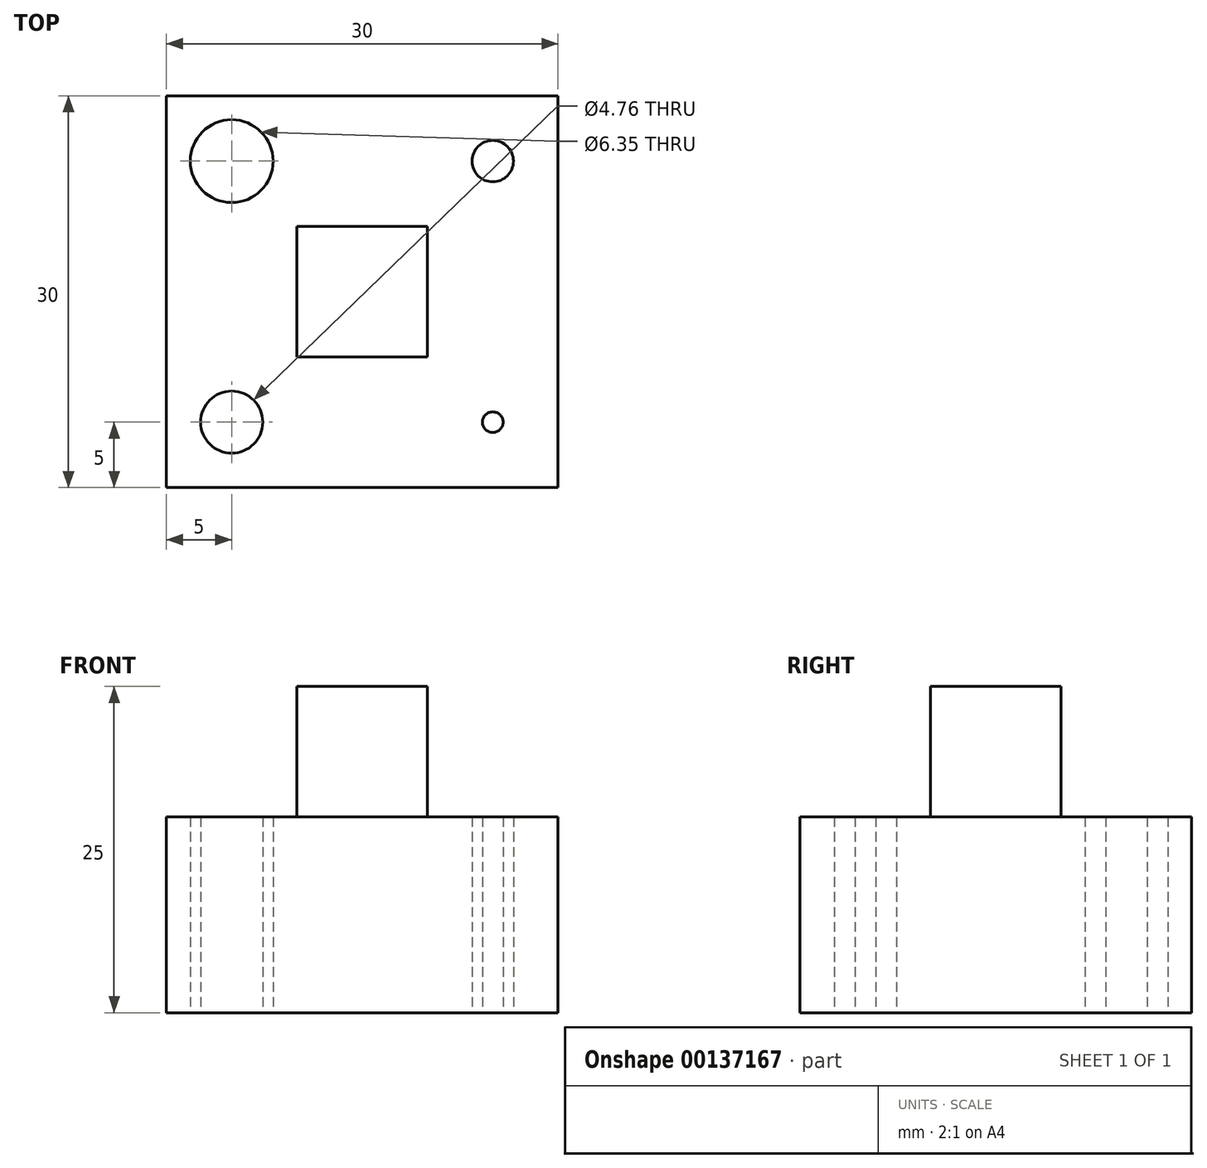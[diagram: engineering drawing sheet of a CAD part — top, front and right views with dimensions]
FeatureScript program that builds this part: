
annotation { "Feature Type Name" : "Feature", "Feature Type Description" : "" }
export const myFeature = defineFeature(function(context is Context, id is Id, definition is map)
    precondition{}
    {
        {
            var Q0;
            Q0=qCreatedBy(makeId("Top.planeOp"),FACE);
            var sketch = newSketch(context, id + "F0", { "sketchPlane" : qUnion([Q0])});
            skLineSegment(sketch, "E0.bottom", {"start": v(15, 15) * mm, "end": v(-15, 15) * mm});
            skLineSegment(sketch, "E0.top", {"start": v(15, -15) * mm, "end": v(-15, -15) * mm});
            skLineSegment(sketch, "E0.left", {"start": v(15, 15) * mm, "end": v(15, -15) * mm});
            skLineSegment(sketch, "E0.right", {"start": v(-15, 15) * mm, "end": v(-15, -15) * mm});
            skPoint(sketch, "E0.middle", {"position": v(0, 0) * mm});
            skPoint(sketch, "E1", {"position": v(0, 15) * mm});
            skCircle(sketch, "E2", {"center": v(-10, 10) * mm, "radius": 3.18 * mm});
            skCircle(sketch, "E3", {"center": v(-10, -10) * mm, "radius": 2.38 * mm});
            skCircle(sketch, "E4", {"center": v(10, 10) * mm, "radius": 1.59 * mm});
            skCircle(sketch, "E5", {"center": v(10, -10) * mm, "radius": 0.8 * mm});
            skLineSegment(sketch, "E6.bottom", {"start": v(10, 10) * mm, "end": v(-10, 10) * mm, "construction": true});
            skLineSegment(sketch, "E6.top", {"start": v(10, -10) * mm, "end": v(-10, -10) * mm, "construction": true});
            skLineSegment(sketch, "E6.left", {"start": v(10, 10) * mm, "end": v(10, -10) * mm, "construction": true});
            skLineSegment(sketch, "E6.right", {"start": v(-10, 10) * mm, "end": v(-10, -10) * mm, "construction": true});
            skLineSegment(sketch, "E7", {"start": v(-10, 15) * mm, "end": v(-10, 10) * mm, "construction": true});
            skLineSegment(sketch, "E8", {"start": v(-10, 10) * mm, "end": v(-15, 10) * mm, "construction": true});
            skLineSegment(sketch, "E9.bottom", {"start": v(5, 5) * mm, "end": v(-5, 5) * mm});
            skLineSegment(sketch, "E9.top", {"start": v(5, -5) * mm, "end": v(-5, -5) * mm});
            skLineSegment(sketch, "E9.left", {"start": v(5, 5) * mm, "end": v(5, -5) * mm});
            skLineSegment(sketch, "E9.right", {"start": v(-5, 5) * mm, "end": v(-5, -5) * mm});
            skSolve(sketch);
        }
        {
            var Q0;
            Q0 = qSketchRegion(id + "F0", true);
            var Q1;
            Q1=makeQuery(id+"F0.imprint","IMPRINT",FACE,{"disambiguationData":[TD([[makeQuery(id+"F0.imprint","IMPRINT",EDGE,{"derivedFrom":sQuery(id+"F0.wireOp",EDGE,"E9.bottom")}),1.0]])]});
            extrude(context, id + "F1", {"entities" : qUnion([Q0, Q1]), "depth" : 15 * mm});
        }
        {
            var Q0;
            Q0=makeQuery(id+"F0.imprint","IMPRINT",FACE,{"disambiguationData":[TD([[makeQuery(id+"F0.imprint","IMPRINT",EDGE,{"derivedFrom":sQuery(id+"F0.wireOp",EDGE,"E9.bottom")}),1.0]])]});
            extrude(context, id + "F2", {"entities" : qUnion([Q0]), "operationType" : NewBodyOperationType.ADD, "depth" : 25 * mm});
        }
    });
